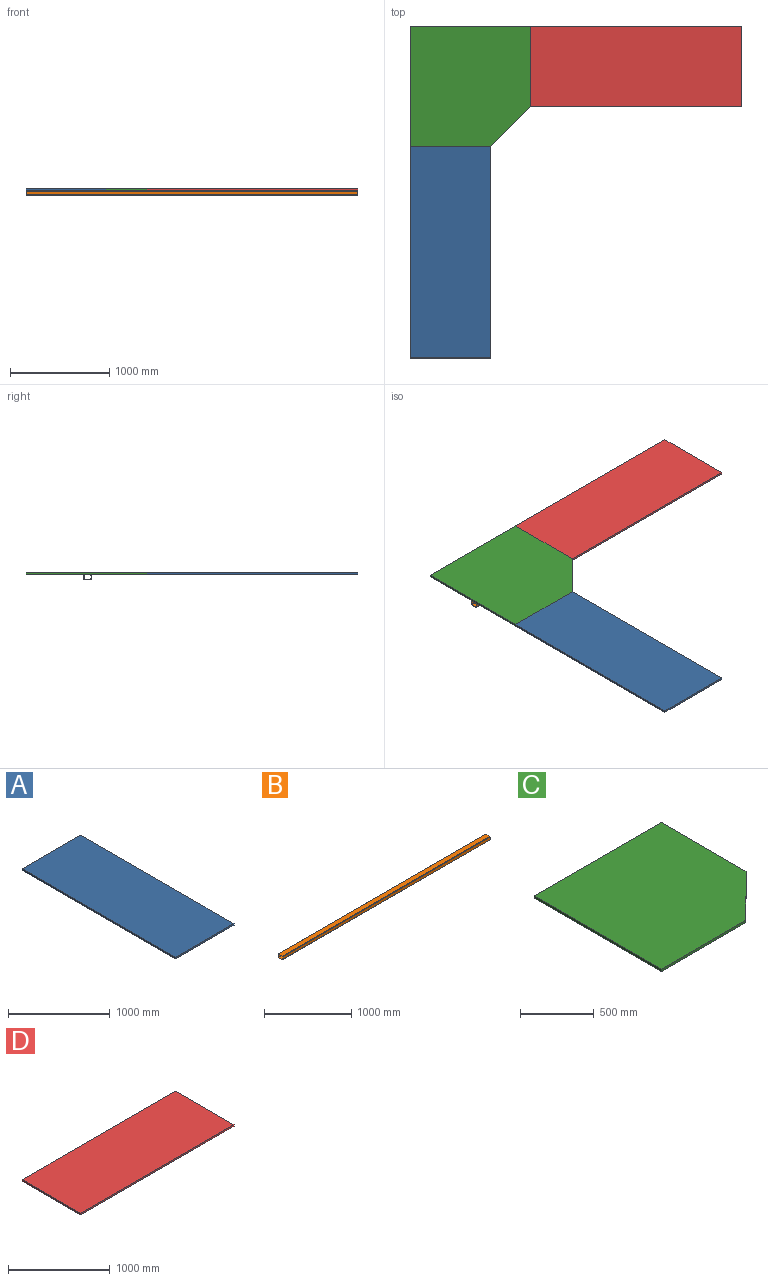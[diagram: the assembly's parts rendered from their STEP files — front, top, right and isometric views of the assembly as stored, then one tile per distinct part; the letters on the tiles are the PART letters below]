
ASSEMBLY  parts=4 mates=5
PART A: 6 faces, bbox 812.8x2133.6x19.1 mm
  f0: plane 812.8x19.05mm, normal (0,1,0), area 15483.8mm2, adj f1,f3,f4,f5
  f1: plane 2133.6x19.05mm, normal (-1,0,0), area 40645.1mm2, adj f0,f2,f4,f5
  f2: plane 812.8x19.05mm, normal (0,-1,0), area 15483.8mm2, adj f1,f3,f4,f5
  f3: plane 2133.6x19.05mm, normal (1,0,0), area 40645.1mm2, adj f0,f2,f4,f5
  f4: plane 2133.6x812.8mm, normal (0,0,1), area 1734190.1mm2, adj f0,f1,f2,f3
  f5: plane 2133.6x812.8mm, normal (0,0,-1), area 1734190.1mm2, adj f0,f1,f2,f3
PART B: 18 faces, bbox 3352.8x76.2x50.8 mm
  f0: plane 76.2x50.8mm, normal (-1,0,0), area 766.1mm2, adj f1,f2,f3,f4,f5,f6,f7,f8
  f1: plane 3352.8x63.5mm, normal (0,0,1), area 212902.8mm2, adj f0,f2,f16,f17
  f2: cylinder r=6.35mm len=3352.8mm, axis (1,0,0), area 33442.7mm2, adj f0,f1,f3,f17
  f3: plane 3352.8x38.1mm, normal (0,-1,0), area 127741.7mm2, adj f0,f2,f4,f17
  f4: cylinder r=6.35mm len=3352.8mm, axis (1,0,0), area 33442.7mm2, adj f0,f3,f5,f17
  f5: plane 3352.8x63.5mm, normal (0,0,-1), area 212902.8mm2, adj f0,f4,f6,f17
  f6: cylinder r=6.35mm len=3352.8mm, axis (1,0,0), area 33442.7mm2, adj f0,f5,f7,f17
  f7: plane 3352.8x38.1mm, normal (0,1,0), area 127741.7mm2, adj f0,f6,f16,f17
  f8: plane 3352.8x31.75mm, normal (0,-1,0), area 106451.4mm2, adj f0,f9,f15,f17
  f9: cylinder r=6.35mm len=3352.8mm, axis (1,0,0), area 33442.7mm2, adj f0,f8,f10,f17
  f10: plane 3352.8x57.15mm, normal (0,0,1), area 191612.5mm2, adj f0,f9,f11,f17
  f11: cylinder r=6.35mm len=3352.8mm, axis (1,0,0), area 33442.7mm2, adj f0,f10,f12,f17
  f12: plane 3352.8x31.75mm, normal (0,1,0), area 106451.4mm2, adj f0,f11,f13,f17
  f13: cylinder r=6.35mm len=3352.8mm, axis (1,0,0), area 33442.7mm2, adj f0,f12,f14,f17
  f14: plane 3352.8x57.15mm, normal (0,0,-1), area 191612.5mm2, adj f0,f13,f15,f17
  f15: cylinder r=6.35mm len=3352.8mm, axis (1,0,0), area 33442.7mm2, adj f0,f8,f14,f17
  f16: cylinder r=6.35mm len=3352.8mm, axis (1,0,0), area 33442.7mm2, adj f0,f1,f7,f17
  f17: plane 76.2x50.8mm, normal (1,0,0), area 766.1mm2, adj f1,f2,f3,f4,f5,f6,f7,f8
PART C: 7 faces, bbox 1219.2x1219.2x19.1 mm
  f0: plane 406.4x406.4mm, normal (0.71,-0.71,0), area 10948.7mm2, adj f1,f4,f5,f6
  f1: plane 812.8x19.05mm, normal (1,0,0), area 15483.8mm2, adj f0,f2,f5,f6
  f2: plane 1219.2x19.05mm, normal (0,1,0), area 23225.8mm2, adj f1,f3,f5,f6
  f3: plane 1219.2x19.05mm, normal (-1,0,0), area 23225.8mm2, adj f2,f4,f5,f6
  f4: plane 812.8x19.05mm, normal (0,-1,0), area 15483.8mm2, adj f0,f3,f5,f6
  f5: plane 1219.2x1219.2mm, normal (0,0,1), area 1403868.2mm2, adj f0,f1,f2,f3,f4
  f6: plane 1219.2x1219.2mm, normal (0,0,-1), area 1403868.2mm2, adj f0,f1,f2,f3,f4
PART D: 6 faces, bbox 2133.6x812.8x19.1 mm
  f0: plane 812.8x19.05mm, normal (-1,0,0), area 15483.8mm2, adj f1,f3,f4,f5
  f1: plane 2133.6x19.05mm, normal (0,-1,0), area 40645.1mm2, adj f0,f2,f4,f5
  f2: plane 812.8x19.05mm, normal (1,0,0), area 15483.8mm2, adj f1,f3,f4,f5
  f3: plane 2133.6x19.05mm, normal (0,1,0), area 40645.1mm2, adj f0,f2,f4,f5
  f4: plane 2133.6x812.8mm, normal (0,0,1), area 1734190.1mm2, adj f0,f1,f2,f3
  f5: plane 2133.6x812.8mm, normal (0,0,-1), area 1734190.1mm2, adj f0,f1,f2,f3
PLACE A t=(-1121.89,1417.89,-1596.93)mm
PLACE B t=(-1121.89,1417.89,-1596.93)mm
PLACE C t=(-1121.89,1417.89,-1596.93)mm
PLACE D t=(-1121.89,1417.89,-1596.93)mm
MATE parallel D.f1 <-> B.f3  axis (0,-1,0) through (2230.91,605.09,-673)mm
MATE parallel B.f17 <-> D.f2  axis (1,0,0) through (2230.91,795.59,-682.53)mm
MATE planar D.f5 <-> B.f1  axis (0,0,-1) through (1164.11,1011.49,-682.53)mm
MATE fastened D.f0 <-> C.f1  axis (-1,0,0) through (97.31,605.09,-663.48)mm
MATE fastened A.f0 <-> C.f4  axis (0,1,0) through (-309.09,198.69,-663.48)mm
